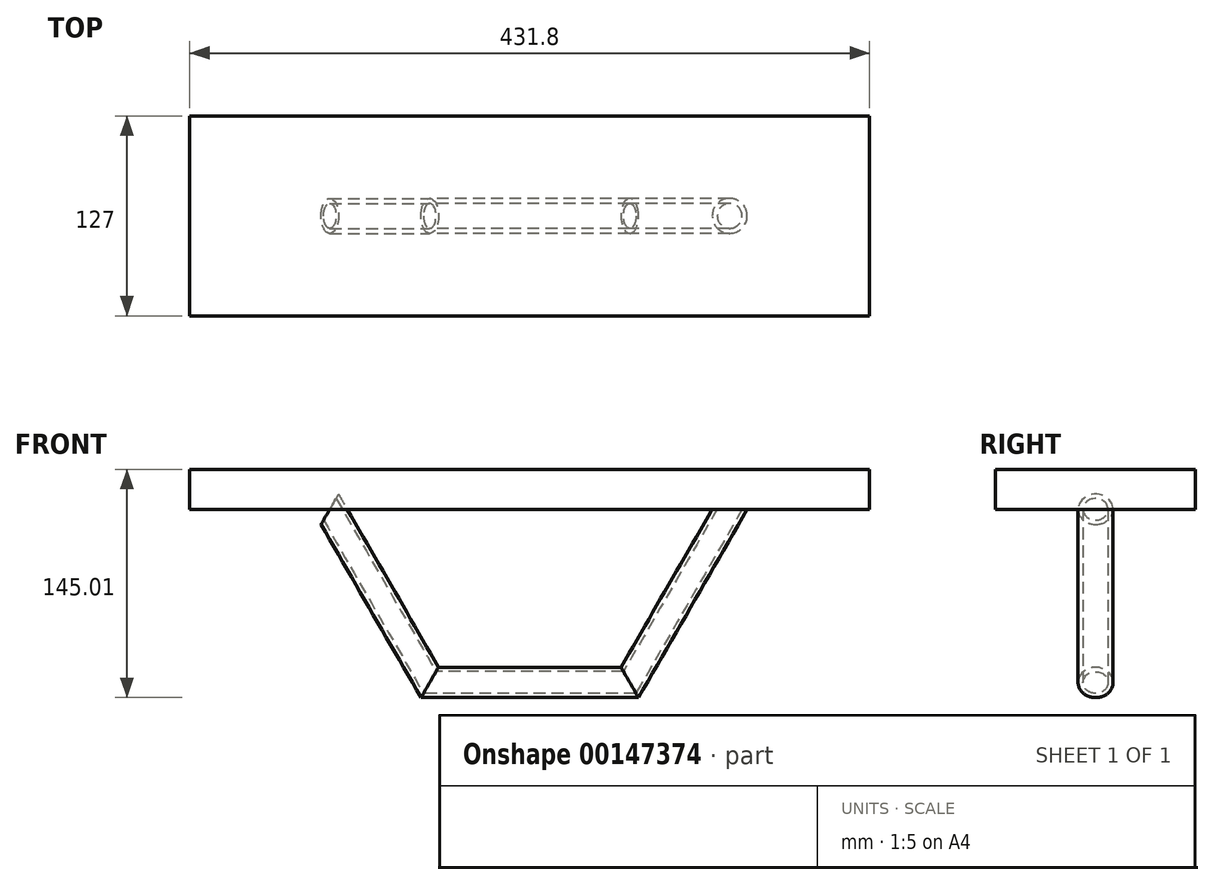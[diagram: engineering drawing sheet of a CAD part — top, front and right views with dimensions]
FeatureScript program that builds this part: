
annotation { "Feature Type Name" : "Feature", "Feature Type Description" : "" }
export const myFeature = defineFeature(function(context is Context, id is Id, definition is map)
    precondition{}
    {
        {
            var Q0;
            Q0=qCreatedBy(makeId("Top.planeOp"),FACE);
            var sketch = newSketch(context, id + "F0", { "sketchPlane" : qUnion([Q0])});
            skLineSegment(sketch, "E0.bottom", {"start": v(215.9, -63.5) * mm, "end": v(-215.9, -63.5) * mm});
            skLineSegment(sketch, "E0.top", {"start": v(215.9, 63.5) * mm, "end": v(-215.9, 63.5) * mm});
            skLineSegment(sketch, "E0.left", {"start": v(215.9, -63.5) * mm, "end": v(215.9, 63.5) * mm});
            skLineSegment(sketch, "E0.right", {"start": v(-215.9, -63.5) * mm, "end": v(-215.9, 63.5) * mm});
            skPoint(sketch, "E0.middle", {"position": v(0, 0) * mm});
            skCircle(sketch, "E1", {"center": v(-127, 0) * mm, "radius": 11.11 * mm});
            skCircle(sketch, "E2", {"center": v(127, 0) * mm, "radius": 11.11 * mm});
            skCircle(sketch, "E3", {"center": v(127, 0) * mm, "radius": 7.94 * mm});
            skCircle(sketch, "E4", {"center": v(-127, 0) * mm, "radius": 7.94 * mm});
            skSolve(sketch);
        }
        {
            var Q0;
            Q0=makeQuery(id+"F0.imprint","IMPRINT",FACE,{"disambiguationData":[TD([[makeQuery(id+"F0.imprint","IMPRINT",EDGE,{"derivedFrom":sQuery(id+"F0.wireOp",EDGE,"E0.bottom")}),-1.0]])]});
            var Q1;
            Q1=makeQuery(id+"F0.imprint","IMPRINT",FACE,{"disambiguationData":[TD([[makeQuery(id+"F0.imprint","IMPRINT",EDGE,{"derivedFrom":sQuery(id+"F0.wireOp",EDGE,"E1")}),1.0]])]});
            var Q2;
            Q2=makeQuery(id+"F0.imprint","IMPRINT",FACE,{"disambiguationData":[TD([[makeQuery(id+"F0.imprint","IMPRINT",EDGE,{"derivedFrom":sQuery(id+"F0.wireOp",EDGE,"E2")}),1.0]])]});
            var Q3;
            Q3=makeQuery(id+"F0.imprint","IMPRINT",FACE,{"disambiguationData":[TD([[makeQuery(id+"F0.imprint","IMPRINT",EDGE,{"derivedFrom":sQuery(id+"F0.wireOp",EDGE,"E3")}),1.0]])]});
            var Q4;
            Q4=makeQuery(id+"F0.imprint","IMPRINT",FACE,{"disambiguationData":[TD([[makeQuery(id+"F0.imprint","IMPRINT",EDGE,{"derivedFrom":sQuery(id+"F0.wireOp",EDGE,"E4")}),1.0]])]});
            extrude(context, id + "F1", {"entities" : qUnion([Q0, Q1, Q2, Q3, Q4]), "depth" : 25.4 * mm});
        }
        {
            var Q0;
            Q0=qCreatedBy(makeId("Front.planeOp"),FACE);
            var sketch = newSketch(context, id + "F2", { "sketchPlane" : qUnion([Q0])});
            skLineSegment(sketch, "E5", {"start": v(-127, 0) * mm, "end": v(-63.5, -109.99) * mm});
            skLineSegment(sketch, "E6", {"start": v(-63.5, -109.99) * mm, "end": v(63.5, -109.99) * mm});
            skLineSegment(sketch, "E7", {"start": v(63.5, -109.99) * mm, "end": v(127, 0) * mm});
            skSolve(sketch);
        }
        {
            var Q0;
            Q0=makeQuery(id+"F0.imprint","IMPRINT",FACE,{"disambiguationData":[TD([[makeQuery(id+"F0.imprint","IMPRINT",EDGE,{"derivedFrom":sQuery(id+"F0.wireOp",EDGE,"E2")}),1.0]])]});
            var Q1;
            Q1=sQuery(id+"F2.wireOp",EDGE,"E6");
            var Q2;
            Q2=sQuery(id+"F2.wireOp",EDGE,"E7");
            var Q3;
            Q3=sQuery(id+"F2.wireOp",EDGE,"E5");
            sweep(context, id + "F3", {"profiles" : qUnion([Q0]), "path" : qUnion([Q1, Q2, Q3])});
        }
    });
